# Revit family: JC KONTAKTER JCK277 DE
name_source: partatom
category: Specialty Equipment
units: mm (PartAtom-declared; Revit-internal decimal feet)

## family parameters
Cut with Voids When Loaded = No
Enable Cutting in Views = Yes
Host = Face
Maintain Annotation Orientation = Yes
Part Type = Normal
Room Calculation Point = No
Round Connector Dimension = Use Diameter
Shared = No

## types (1)
- JCK277
    Anzahl der mikroschalter = 2
    CE-kennzeichnung = https://jckontakter.se
    Deckel = Aluminum 6060-T6 (Schwarz)
    Default Elevation = 800 mm  [stored 2.62467 ft]
    Description = JCK277 ist ein modernes Modell, ausgestattet mit einem führenden LED-Licht (blau). Das Modell verfügt außerdem über eine versenkte taktile Rille, um die Nutzung für Sehbehinderte zu erleichtern. Hergestellt aus schwarzeloxiertem Aluminium mit schwarzen Endkappen.
    Endkappen = POM Tenac C 4520
    Geringster nennstrom = 1mA/4 V DC
    Herstellungsland = Schweden
    Kern = Aluminum 6060-T6
    Linse = Acryl
    Manufacturer = JC kontakter
    Mikroschalter = Standard NO IP67
    Model = JCK277
    Nomineller nennstrom = 12 V Resistiv 6A Induktiv L/R 5 ms 6A, 24 V Resistiv 6A Induktiv L/R 5 ms 5A
    Produktgewicht = 0.310 kg.
    Technisches Produktblatt = https://grossflaechentaster.de
    URL = https://grossflaechentaster.de

note: [stored X ft] marks values corroborated as IEEE doubles in the binary element streams (Revit-internal decimal feet)

## geometry (parser evidence)
native form markers: Sweep x4
no freeform markers — native parametric forms only
